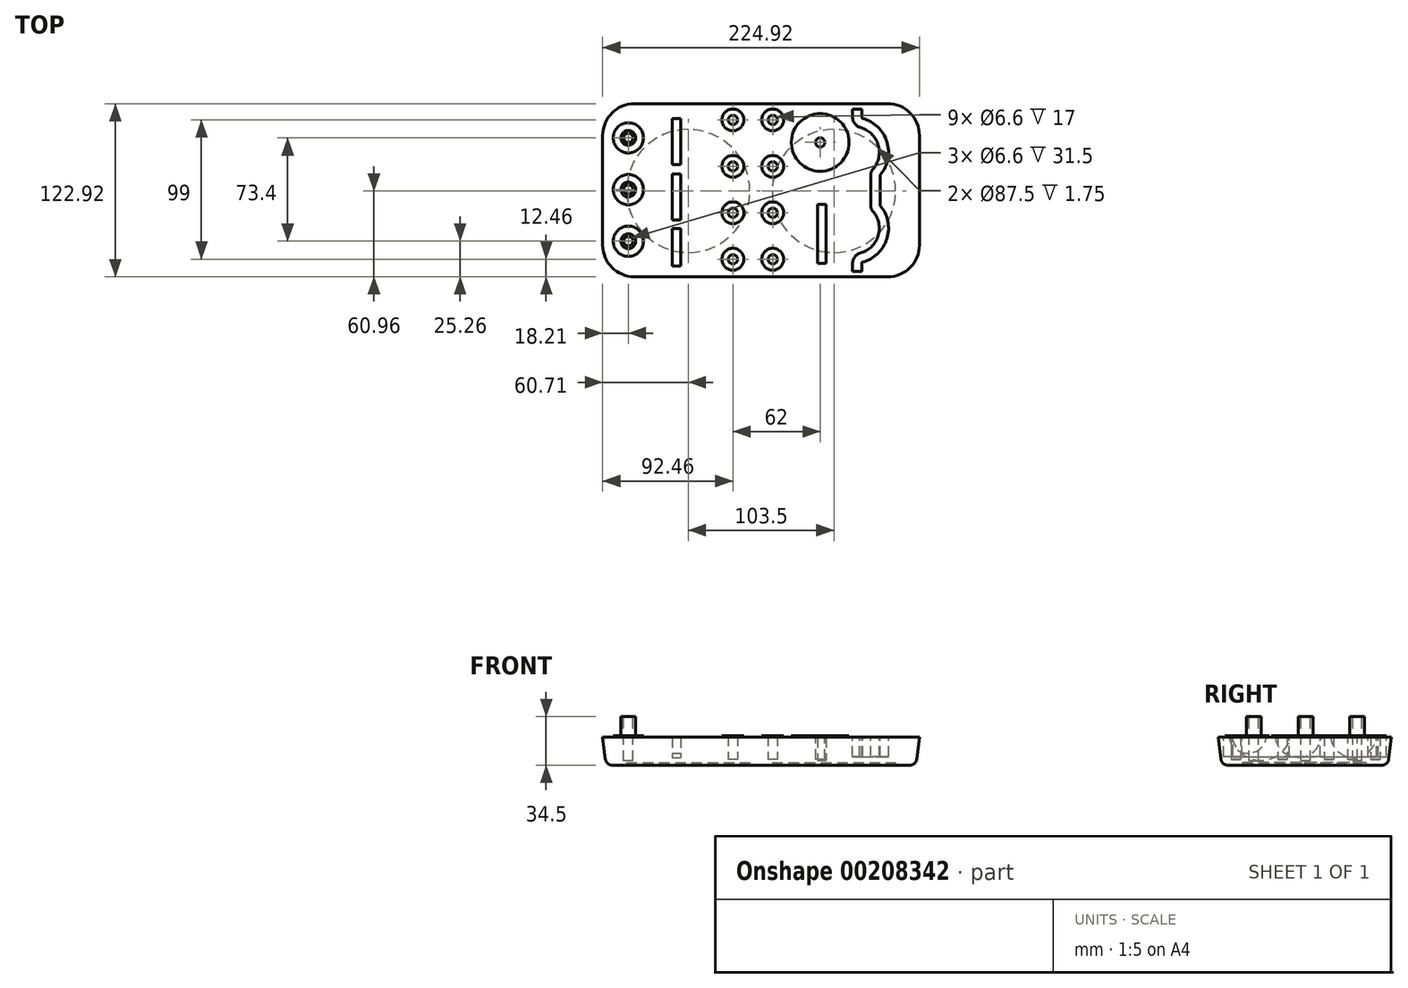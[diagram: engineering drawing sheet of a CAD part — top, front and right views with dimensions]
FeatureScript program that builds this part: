
annotation { "Feature Type Name" : "Feature", "Feature Type Description" : "" }
export const myFeature = defineFeature(function(context is Context, id is Id, definition is map)
    precondition{}
    {
        {
            var Q0;
            Q0=qCreatedBy(makeId("Top.planeOp"),FACE);
            var sketch = newSketch(context, id + "F0", { "sketchPlane" : qUnion([Q0])});
            skLineSegment(sketch, "E0.bottom", {"start": v(20, 0) * mm, "end": v(200, 0) * mm});
            skLineSegment(sketch, "E0.top", {"start": v(20, 118) * mm, "end": v(200, 118) * mm});
            skLineSegment(sketch, "E0.left", {"start": v(0, 20) * mm, "end": v(0, 98) * mm});
            skLineSegment(sketch, "E0.right", {"start": v(220, 20) * mm, "end": v(220, 98) * mm});
            skPoint(sketch, "E1.visualSharp", {"position": v(0, 118) * mm});
            skArc(sketch, "E1.filletArc", {"start": v(20, 118) * mm, "mid": v(5.86, 112.14) * mm, "end": v(0, 98) * mm});
            skPoint(sketch, "E2.visualSharp", {"position": v(220, 118) * mm});
            skArc(sketch, "E2.filletArc", {"start": v(220, 98) * mm, "mid": v(214.14, 112.14) * mm, "end": v(200, 118) * mm});
            skPoint(sketch, "E3.visualSharp", {"position": v(0, 0) * mm});
            skArc(sketch, "E3.filletArc", {"start": v(0, 20) * mm, "mid": v(5.86, 5.86) * mm, "end": v(20, 0) * mm});
            skPoint(sketch, "E4.visualSharp", {"position": v(220, 0) * mm});
            skArc(sketch, "E4.filletArc", {"start": v(200, 0) * mm, "mid": v(214.14, 5.86) * mm, "end": v(220, 20) * mm});
            skSolve(sketch);
        }
        {
            var Q0;
            Q0=makeQuery(id+"F0.imprint","IMPRINT",FACE,{"disambiguationData":[TD([[makeQuery(id+"F0.imprint","IMPRINT",EDGE,{"derivedFrom":sQuery(id+"F0.wireOp",EDGE,"E0.bottom")}),1.0]])]});
            extrude(context, id + "F1", {"entities" : qUnion([Q0]), "depth" : 20 * mm, "hasDraft" : true, "draftAngle" : 7 * degree});
        }
        {
            var Q0;
            Q0=makeQuery(id+"F1.opExtrude","CAP_FACE",FACE,{"disambiguationData":[OSD([sQuery(id+"F0.wireOp",EDGE,"E0.bottom"),sQuery(id+"F0.wireOp",EDGE,"E0.top"),sQuery(id+"F0.wireOp",EDGE,"E0.left"),sQuery(id+"F0.wireOp",EDGE,"E0.right"),sQuery(id+"F0.wireOp",EDGE,"E1.filletArc"),sQuery(id+"F0.wireOp",EDGE,"E2.filletArc"),sQuery(id+"F0.wireOp",EDGE,"E3.filletArc"),sQuery(id+"F0.wireOp",EDGE,"E4.filletArc")])],"isStart":true});
            fillet(context, id + "F2", {"entities" : qUnion([Q0]), "radius" : 5 * mm, "tangentPropagation" : true, "allowEdgeOverflow" : false});
        }
        {
            var Q0;
            Q0=makeQuery(id+"F1.opExtrude","CAP_FACE",FACE,{"disambiguationData":[OSD([sQuery(id+"F0.wireOp",EDGE,"E0.bottom"),sQuery(id+"F0.wireOp",EDGE,"E0.top"),sQuery(id+"F0.wireOp",EDGE,"E0.left"),sQuery(id+"F0.wireOp",EDGE,"E0.right"),sQuery(id+"F0.wireOp",EDGE,"E1.filletArc"),sQuery(id+"F0.wireOp",EDGE,"E2.filletArc"),sQuery(id+"F0.wireOp",EDGE,"E3.filletArc"),sQuery(id+"F0.wireOp",EDGE,"E4.filletArc")])],"isStart":true});
            var sketch = newSketch(context, id + "F3", { "sketchPlane" : qUnion([Q0])});
            skLineSegment(sketch, "E5.bottom", {"start": v(0, 0) * mm, "end": v(58.25, 0) * mm, "construction": true});
            skLineSegment(sketch, "E5.top", {"start": v(0, -58.5) * mm, "end": v(58.25, -58.5) * mm, "construction": true});
            skLineSegment(sketch, "E5.left", {"start": v(0, 0) * mm, "end": v(0, -58.5) * mm, "construction": true});
            skLineSegment(sketch, "E5.right", {"start": v(58.25, 0) * mm, "end": v(58.25, -58.5) * mm, "construction": true});
            skLineSegment(sketch, "E6.bottom", {"start": v(0, 0) * mm, "end": v(161.75, 0) * mm, "construction": true});
            skLineSegment(sketch, "E6.top", {"start": v(0, -58.5) * mm, "end": v(161.75, -58.5) * mm, "construction": true});
            skLineSegment(sketch, "E6.right", {"start": v(161.75, 0) * mm, "end": v(161.75, -58.5) * mm, "construction": true});
            skCircle(sketch, "E7", {"center": v(58.25, -58.5) * mm, "radius": 43.75 * mm});
            skCircle(sketch, "E8", {"center": v(161.75, -58.5) * mm, "radius": 43.75 * mm});
            skSolve(sketch);
        }
        {
            var Q0;
            Q0=qSketchRegion(id+"F3",true);
            extrude(context, id + "F4", {"entities" : qUnion([Q0]), "operationType" : NewBodyOperationType.REMOVE, "oppositeDirection" : true, "depth" : 1.75 * mm});
        }
        {
            var Q0;
            Q0=makeQuery(id+"F1.opExtrude","CAP_FACE",FACE,{"disambiguationData":[OSD([sQuery(id+"F0.wireOp",EDGE,"E0.bottom"),sQuery(id+"F0.wireOp",EDGE,"E0.top"),sQuery(id+"F0.wireOp",EDGE,"E0.left"),sQuery(id+"F0.wireOp",EDGE,"E0.right"),sQuery(id+"F0.wireOp",EDGE,"E1.filletArc"),sQuery(id+"F0.wireOp",EDGE,"E2.filletArc"),sQuery(id+"F0.wireOp",EDGE,"E3.filletArc"),sQuery(id+"F0.wireOp",EDGE,"E4.filletArc")])],"isStart":false});
            var sketch = newSketch(context, id + "F5", { "sketchPlane" : qUnion([Q0])});
            skLineSegment(sketch, "E9.bottom", {"start": v(0, 0) * mm, "end": v(15.75, 0) * mm, "construction": true});
            skLineSegment(sketch, "E9.top", {"start": v(0, 59.5) * mm, "end": v(15.75, 59.5) * mm, "construction": true});
            skLineSegment(sketch, "E9.left", {"start": v(0, 0) * mm, "end": v(0, 59.5) * mm, "construction": true});
            skLineSegment(sketch, "E9.right", {"start": v(15.75, 0) * mm, "end": v(15.75, 59.5) * mm, "construction": true});
            skLineSegment(sketch, "E10", {"start": v(15.75, 59.5) * mm, "end": v(15.75, 22.8) * mm, "construction": true});
            skLineSegment(sketch, "E11", {"start": v(15.75, 59.5) * mm, "end": v(15.75, 96.2) * mm, "construction": true});
            skCircle(sketch, "E12", {"center": v(15.75, 96.2) * mm, "radius": 10.75 * mm});
            skCircle(sketch, "E13", {"center": v(15.75, 59.5) * mm, "radius": 10.75 * mm});
            skCircle(sketch, "E14", {"center": v(15.75, 22.8) * mm, "radius": 10.75 * mm});
            skCircle(sketch, "E15", {"center": v(15.75, 96.2) * mm, "radius": 3.3 * mm});
            skCircle(sketch, "E16", {"center": v(15.75, 96.2) * mm, "radius": 5.25 * mm});
            skCircle(sketch, "E17", {"center": v(15.75, 59.5) * mm, "radius": 5.25 * mm});
            skCircle(sketch, "E18", {"center": v(15.75, 59.5) * mm, "radius": 3.3 * mm});
            skCircle(sketch, "E19", {"center": v(15.75, 22.8) * mm, "radius": 5.25 * mm});
            skCircle(sketch, "E20", {"center": v(15.75, 22.8) * mm, "radius": 3.3 * mm});
            skSolve(sketch);
        }
        {
            var Q0;
            Q0=makeQuery(id+"F5.imprint","IMPRINT",FACE,{"disambiguationData":[TD([[makeQuery(id+"F5.imprint","IMPRINT",EDGE,{"derivedFrom":sQuery(id+"F5.wireOp",EDGE,"E20")}),1.0]])]});
            var Q1;
            Q1=makeQuery(id+"F5.imprint","IMPRINT",FACE,{"disambiguationData":[TD([[makeQuery(id+"F5.imprint","IMPRINT",EDGE,{"derivedFrom":sQuery(id+"F5.wireOp",EDGE,"E18")}),1.0]])]});
            var Q2;
            Q2=makeQuery(id+"F5.imprint","IMPRINT",FACE,{"disambiguationData":[TD([[makeQuery(id+"F5.imprint","IMPRINT",EDGE,{"derivedFrom":sQuery(id+"F5.wireOp",EDGE,"E15")}),1.0]])]});
            extrude(context, id + "F6", {"entities" : qUnion([Q0, Q1, Q2]), "operationType" : NewBodyOperationType.REMOVE, "oppositeDirection" : true, "depth" : 17 * mm});
        }
        {
            var Q0;
            Q0=makeQuery(id+"F5.imprint","IMPRINT",FACE,{"disambiguationData":[TD([[makeQuery(id+"F5.imprint","IMPRINT",EDGE,{"derivedFrom":sQuery(id+"F5.wireOp",EDGE,"E19")}),1.0]])]});
            var Q1;
            Q1=makeQuery(id+"F5.imprint","IMPRINT",FACE,{"disambiguationData":[TD([[makeQuery(id+"F5.imprint","IMPRINT",EDGE,{"derivedFrom":sQuery(id+"F5.wireOp",EDGE,"E17")}),1.0]])]});
            var Q2;
            Q2=makeQuery(id+"F5.imprint","IMPRINT",FACE,{"disambiguationData":[TD([[makeQuery(id+"F5.imprint","IMPRINT",EDGE,{"derivedFrom":sQuery(id+"F5.wireOp",EDGE,"E15")}),-1.0]])]});
            extrude(context, id + "F7", {"entities" : qUnion([Q0, Q1, Q2]), "operationType" : NewBodyOperationType.ADD, "depth" : 14.5 * mm});
        }
        {
            var Q0;
            Q0=makeQuery(id+"F5.imprint","IMPRINT",FACE,{"disambiguationData":[TD([[makeQuery(id+"F5.imprint","IMPRINT",EDGE,{"derivedFrom":sQuery(id+"F5.wireOp",EDGE,"E12")}),1.0]])]});
            var Q1;
            Q1=makeQuery(id+"F5.imprint","IMPRINT",FACE,{"disambiguationData":[TD([[makeQuery(id+"F5.imprint","IMPRINT",EDGE,{"derivedFrom":sQuery(id+"F5.wireOp",EDGE,"E13")}),1.0]])]});
            var Q2;
            Q2=makeQuery(id+"F5.imprint","IMPRINT",FACE,{"disambiguationData":[TD([[makeQuery(id+"F5.imprint","IMPRINT",EDGE,{"derivedFrom":sQuery(id+"F5.wireOp",EDGE,"E14")}),1.0]])]});
            extrude(context, id + "F8", {"entities" : qUnion([Q0, Q1, Q2]), "operationType" : NewBodyOperationType.ADD, "depth" : 1 * mm});
        }
        {
            var Q0;
            Q0=qCreatedBy(makeId("Top.planeOp"),FACE);
            cPlane(context, id + "F9", {"entities" : qUnion([Q0]), "cplaneType" : CPlaneType.OFFSET, "offset" : 22 * mm, "width" : 150 * mm, "height" : 150 * mm});
        }
        {
            var Q0;
            Q0=qCreatedBy(id+"F9.planeOp",FACE);
            var sketch = newSketch(context, id + "F10", { "sketchPlane" : qUnion([Q0])});
            skLineSegment(sketch, "E21.bottom", {"start": v(0, 0) * mm, "end": v(47, 0) * mm, "construction": true});
            skLineSegment(sketch, "E21.top", {"start": v(0, 54.3) * mm, "end": v(47, 54.3) * mm, "construction": true});
            skLineSegment(sketch, "E21.left", {"start": v(0, 0) * mm, "end": v(0, 54.3) * mm, "construction": true});
            skLineSegment(sketch, "E21.right", {"start": v(47, 0) * mm, "end": v(47, 54.3) * mm, "construction": true});
            skLineSegment(sketch, "E22.bottom", {"start": v(47, 54.3) * mm, "end": v(53, 54.3) * mm});
            skLineSegment(sketch, "E22.top", {"start": v(47, 70.8) * mm, "end": v(53, 70.8) * mm});
            skLineSegment(sketch, "E22.left", {"start": v(47, 54.3) * mm, "end": v(47, 70.8) * mm});
            skLineSegment(sketch, "E22.right", {"start": v(53, 54.3) * mm, "end": v(53, 70.8) * mm});
            skSolve(sketch);
        }
        {
            var Q0;
            Q0=makeQuery(id+"F10.imprint","IMPRINT",FACE,{"disambiguationData":[TD([[makeQuery(id+"F10.imprint","IMPRINT",EDGE,{"derivedFrom":sQuery(id+"F10.wireOp",EDGE,"E22.bottom")}),1.0]])]});
            var Q1;
            Q1=sQuery(id+"F10.wireOp",EDGE,"E22.bottom");
            revolve(context, id + "F11", {"operationType" : NewBodyOperationType.REMOVE, "entities" : qUnion([Q0]), "axis" : qUnion([Q1]), "revolveType" : RevolveType.FULL, "oppositeDirection" : true});
        }
        {
            var Q0;
            Q0=qCreatedBy(id+"F9.planeOp",FACE);
            var sketch = newSketch(context, id + "F12", { "sketchPlane" : qUnion([Q0])});
            skLineSegment(sketch, "E23.bottom", {"start": v(0, 0) * mm, "end": v(47, 0) * mm, "construction": true});
            skLineSegment(sketch, "E23.top", {"start": v(0, 18.5) * mm, "end": v(47, 18.5) * mm, "construction": true});
            skLineSegment(sketch, "E23.left", {"start": v(0, 0) * mm, "end": v(0, 18.5) * mm, "construction": true});
            skLineSegment(sketch, "E23.right", {"start": v(47, 0) * mm, "end": v(47, 18.5) * mm, "construction": true});
            skLineSegment(sketch, "E24.bottom", {"start": v(47, 18.5) * mm, "end": v(53, 18.5) * mm});
            skLineSegment(sketch, "E24.top", {"start": v(47, 32) * mm, "end": v(53, 32) * mm});
            skLineSegment(sketch, "E24.left", {"start": v(47, 18.5) * mm, "end": v(47, 32) * mm});
            skLineSegment(sketch, "E24.right", {"start": v(53, 18.5) * mm, "end": v(53, 32) * mm});
            skSolve(sketch);
        }
        {
            var Q0;
            Q0=makeQuery(id+"F12.imprint","IMPRINT",FACE,{"disambiguationData":[TD([[makeQuery(id+"F12.imprint","IMPRINT",EDGE,{"derivedFrom":sQuery(id+"F12.wireOp",EDGE,"E24.bottom")}),1.0]])]});
            var Q1;
            Q1=sQuery(id+"F12.wireOp",EDGE,"E24.bottom");
            revolve(context, id + "F13", {"operationType" : NewBodyOperationType.REMOVE, "entities" : qUnion([Q0]), "axis" : qUnion([Q1]), "revolveType" : RevolveType.FULL, "oppositeDirection" : true});
        }
        {
            var Q0;
            Q0=qCreatedBy(id+"F9.planeOp",FACE);
            var sketch = newSketch(context, id + "F14", { "sketchPlane" : qUnion([Q0])});
            skLineSegment(sketch, "E25.bottom", {"start": v(0, 0) * mm, "end": v(47, 0) * mm, "construction": true});
            skLineSegment(sketch, "E25.top", {"start": v(0, 93.5) * mm, "end": v(47, 93.5) * mm, "construction": true});
            skLineSegment(sketch, "E25.left", {"start": v(0, 0) * mm, "end": v(0, 93.5) * mm, "construction": true});
            skLineSegment(sketch, "E25.right", {"start": v(47, 0) * mm, "end": v(47, 93.5) * mm, "construction": true});
            skLineSegment(sketch, "E26.bottom", {"start": v(47, 93.5) * mm, "end": v(53, 93.5) * mm});
            skLineSegment(sketch, "E26.top", {"start": v(47, 110) * mm, "end": v(53, 110) * mm});
            skLineSegment(sketch, "E26.left", {"start": v(47, 93.5) * mm, "end": v(47, 110) * mm});
            skLineSegment(sketch, "E26.right", {"start": v(53, 93.5) * mm, "end": v(53, 110) * mm});
            skSolve(sketch);
        }
        {
            var Q0;
            Q0=makeQuery(id+"F14.imprint","IMPRINT",FACE,{"disambiguationData":[TD([[makeQuery(id+"F14.imprint","IMPRINT",EDGE,{"derivedFrom":sQuery(id+"F14.wireOp",EDGE,"E26.bottom")}),1.0]])]});
            var Q1;
            Q1=sQuery(id+"F14.wireOp",EDGE,"E26.bottom");
            revolve(context, id + "F15", {"operationType" : NewBodyOperationType.REMOVE, "entities" : qUnion([Q0]), "axis" : qUnion([Q1]), "revolveType" : RevolveType.FULL, "oppositeDirection" : true});
        }
        {
            var Q0;
            Q0=makeQuery(id+"F1.opExtrude","CAP_FACE",FACE,{"disambiguationData":[OSD([sQuery(id+"F0.wireOp",EDGE,"E0.bottom"),sQuery(id+"F0.wireOp",EDGE,"E0.top"),sQuery(id+"F0.wireOp",EDGE,"E0.left"),sQuery(id+"F0.wireOp",EDGE,"E0.right"),sQuery(id+"F0.wireOp",EDGE,"E1.filletArc"),sQuery(id+"F0.wireOp",EDGE,"E2.filletArc"),sQuery(id+"F0.wireOp",EDGE,"E3.filletArc"),sQuery(id+"F0.wireOp",EDGE,"E4.filletArc")])],"isStart":false});
            var sketch = newSketch(context, id + "F16", { "sketchPlane" : qUnion([Q0])});
            skLineSegment(sketch, "E27.bottom", {"start": v(0, 0) * mm, "end": v(90, 0) * mm, "construction": true});
            skLineSegment(sketch, "E27.top", {"start": v(0, 10) * mm, "end": v(90, 10) * mm, "construction": true});
            skLineSegment(sketch, "E27.left", {"start": v(0, 0) * mm, "end": v(0, 10) * mm, "construction": true});
            skLineSegment(sketch, "E27.right", {"start": v(90, 0) * mm, "end": v(90, 10) * mm, "construction": true});
            skLineSegment(sketch, "E28.bottom", {"start": v(90, 10) * mm, "end": v(118.3, 10) * mm, "construction": true});
            skLineSegment(sketch, "E28.top", {"start": v(90, 43) * mm, "end": v(118.3, 43) * mm, "construction": true});
            skLineSegment(sketch, "E28.left", {"start": v(90, 10) * mm, "end": v(90, 43) * mm, "construction": true});
            skLineSegment(sketch, "E28.right", {"start": v(118.3, 10) * mm, "end": v(118.3, 43) * mm, "construction": true});
            skLineSegment(sketch, "E29.top", {"start": v(90, 76) * mm, "end": v(118.3, 76) * mm, "construction": true});
            skLineSegment(sketch, "E29.left", {"start": v(90, 43) * mm, "end": v(90, 76) * mm, "construction": true});
            skLineSegment(sketch, "E29.right", {"start": v(118.3, 43) * mm, "end": v(118.3, 76) * mm, "construction": true});
            skLineSegment(sketch, "E30.top", {"start": v(90, 109) * mm, "end": v(118.3, 109) * mm, "construction": true});
            skLineSegment(sketch, "E30.left", {"start": v(90, 76) * mm, "end": v(90, 109) * mm, "construction": true});
            skLineSegment(sketch, "E30.right", {"start": v(118.3, 76) * mm, "end": v(118.3, 109) * mm, "construction": true});
            skCircle(sketch, "E31", {"center": v(90, 109) * mm, "radius": 3.3 * mm});
            skCircle(sketch, "E32", {"center": v(118.3, 109) * mm, "radius": 3.3 * mm});
            skCircle(sketch, "E33", {"center": v(118.3, 76) * mm, "radius": 3.3 * mm});
            skCircle(sketch, "E34", {"center": v(90, 76) * mm, "radius": 3.3 * mm});
            skCircle(sketch, "E35", {"center": v(90, 43) * mm, "radius": 3.3 * mm});
            skCircle(sketch, "E36", {"center": v(118.3, 43) * mm, "radius": 3.3 * mm});
            skCircle(sketch, "E37", {"center": v(118.3, 10) * mm, "radius": 3.3 * mm});
            skCircle(sketch, "E38", {"center": v(90, 10) * mm, "radius": 3.3 * mm});
            skCircle(sketch, "E39", {"center": v(90, 109) * mm, "radius": 7.75 * mm});
            skCircle(sketch, "E40", {"center": v(118.3, 109) * mm, "radius": 7.75 * mm});
            skCircle(sketch, "E41", {"center": v(118.3, 76) * mm, "radius": 7.75 * mm});
            skCircle(sketch, "E42", {"center": v(90, 76) * mm, "radius": 7.75 * mm});
            skCircle(sketch, "E43", {"center": v(90, 43) * mm, "radius": 7.75 * mm});
            skCircle(sketch, "E44", {"center": v(118.3, 43) * mm, "radius": 7.75 * mm});
            skCircle(sketch, "E45", {"center": v(118.3, 10) * mm, "radius": 7.75 * mm});
            skCircle(sketch, "E46", {"center": v(90, 10) * mm, "radius": 7.75 * mm});
            skSolve(sketch);
        }
        {
            var Q0;
            Q0=makeQuery(id+"F16.imprint","IMPRINT",FACE,{"disambiguationData":[TD([[makeQuery(id+"F16.imprint","IMPRINT",EDGE,{"derivedFrom":sQuery(id+"F16.wireOp",EDGE,"E31")}),-1.0]])]});
            var Q1;
            Q1=makeQuery(id+"F16.imprint","IMPRINT",FACE,{"disambiguationData":[TD([[makeQuery(id+"F16.imprint","IMPRINT",EDGE,{"derivedFrom":sQuery(id+"F16.wireOp",EDGE,"E32")}),-1.0]])]});
            var Q2;
            Q2=makeQuery(id+"F16.imprint","IMPRINT",FACE,{"disambiguationData":[TD([[makeQuery(id+"F16.imprint","IMPRINT",EDGE,{"derivedFrom":sQuery(id+"F16.wireOp",EDGE,"E33")}),-1.0]])]});
            var Q3;
            Q3=makeQuery(id+"F16.imprint","IMPRINT",FACE,{"disambiguationData":[TD([[makeQuery(id+"F16.imprint","IMPRINT",EDGE,{"derivedFrom":sQuery(id+"F16.wireOp",EDGE,"E34")}),-1.0]])]});
            var Q4;
            Q4=makeQuery(id+"F16.imprint","IMPRINT",FACE,{"disambiguationData":[TD([[makeQuery(id+"F16.imprint","IMPRINT",EDGE,{"derivedFrom":sQuery(id+"F16.wireOp",EDGE,"E35")}),-1.0]])]});
            var Q5;
            Q5=makeQuery(id+"F16.imprint","IMPRINT",FACE,{"disambiguationData":[TD([[makeQuery(id+"F16.imprint","IMPRINT",EDGE,{"derivedFrom":sQuery(id+"F16.wireOp",EDGE,"E36")}),-1.0]])]});
            var Q6;
            Q6=makeQuery(id+"F16.imprint","IMPRINT",FACE,{"disambiguationData":[TD([[makeQuery(id+"F16.imprint","IMPRINT",EDGE,{"derivedFrom":sQuery(id+"F16.wireOp",EDGE,"E37")}),-1.0]])]});
            var Q7;
            Q7=makeQuery(id+"F16.imprint","IMPRINT",FACE,{"disambiguationData":[TD([[makeQuery(id+"F16.imprint","IMPRINT",EDGE,{"derivedFrom":sQuery(id+"F16.wireOp",EDGE,"E38")}),-1.0]])]});
            extrude(context, id + "F17", {"entities" : qUnion([Q0, Q1, Q2, Q3, Q4, Q5, Q6, Q7]), "operationType" : NewBodyOperationType.ADD, "depth" : 1 * mm});
        }
        {
            var Q0;
            Q0=makeQuery(id+"F16.imprint","IMPRINT",FACE,{"disambiguationData":[TD([[makeQuery(id+"F16.imprint","IMPRINT",EDGE,{"derivedFrom":sQuery(id+"F16.wireOp",EDGE,"E31")}),1.0]])]});
            var Q1;
            Q1=makeQuery(id+"F16.imprint","IMPRINT",FACE,{"disambiguationData":[TD([[makeQuery(id+"F16.imprint","IMPRINT",EDGE,{"derivedFrom":sQuery(id+"F16.wireOp",EDGE,"E32")}),1.0]])]});
            var Q2;
            Q2=makeQuery(id+"F16.imprint","IMPRINT",FACE,{"disambiguationData":[TD([[makeQuery(id+"F16.imprint","IMPRINT",EDGE,{"derivedFrom":sQuery(id+"F16.wireOp",EDGE,"E34")}),1.0]])]});
            var Q3;
            Q3=makeQuery(id+"F16.imprint","IMPRINT",FACE,{"disambiguationData":[TD([[makeQuery(id+"F16.imprint","IMPRINT",EDGE,{"derivedFrom":sQuery(id+"F16.wireOp",EDGE,"E33")}),1.0]])]});
            var Q4;
            Q4=makeQuery(id+"F16.imprint","IMPRINT",FACE,{"disambiguationData":[TD([[makeQuery(id+"F16.imprint","IMPRINT",EDGE,{"derivedFrom":sQuery(id+"F16.wireOp",EDGE,"E36")}),1.0]])]});
            var Q5;
            Q5=makeQuery(id+"F16.imprint","IMPRINT",FACE,{"disambiguationData":[TD([[makeQuery(id+"F16.imprint","IMPRINT",EDGE,{"derivedFrom":sQuery(id+"F16.wireOp",EDGE,"E35")}),1.0]])]});
            var Q6;
            Q6=makeQuery(id+"F16.imprint","IMPRINT",FACE,{"disambiguationData":[TD([[makeQuery(id+"F16.imprint","IMPRINT",EDGE,{"derivedFrom":sQuery(id+"F16.wireOp",EDGE,"E38")}),1.0]])]});
            var Q7;
            Q7=makeQuery(id+"F16.imprint","IMPRINT",FACE,{"disambiguationData":[TD([[makeQuery(id+"F16.imprint","IMPRINT",EDGE,{"derivedFrom":sQuery(id+"F16.wireOp",EDGE,"E37")}),1.0]])]});
            extrude(context, id + "F18", {"entities" : qUnion([Q0, Q1, Q2, Q3, Q4, Q5, Q6, Q7]), "operationType" : NewBodyOperationType.REMOVE, "oppositeDirection" : true, "depth" : 16 * mm});
        }
        {
            var Q0;
            Q0=qCreatedBy(makeId("Top.planeOp"),FACE);
            cPlane(context, id + "F19", {"entities" : qUnion([Q0]), "cplaneType" : CPlaneType.OFFSET, "offset" : 25 * mm, "width" : 150 * mm, "height" : 150 * mm});
        }
        {
            var Q0;
            Q0=qCreatedBy(id+"F19.planeOp",FACE);
            var sketch = newSketch(context, id + "F20", { "sketchPlane" : qUnion([Q0])});
            skLineSegment(sketch, "E47.bottom", {"start": v(0, 0) * mm, "end": v(150, 0) * mm, "construction": true});
            skLineSegment(sketch, "E47.top", {"start": v(0, 28) * mm, "end": v(150, 28) * mm, "construction": true});
            skLineSegment(sketch, "E47.left", {"start": v(0, 0) * mm, "end": v(0, 28) * mm, "construction": true});
            skLineSegment(sketch, "E47.right", {"start": v(150, 0) * mm, "end": v(150, 28) * mm, "construction": true});
            skLineSegment(sketch, "E48.bottom", {"start": v(150, 28) * mm, "end": v(156, 28) * mm});
            skLineSegment(sketch, "E48.top", {"start": v(150, 49.5) * mm, "end": v(156, 49.5) * mm});
            skLineSegment(sketch, "E48.left", {"start": v(150, 28) * mm, "end": v(150, 49.5) * mm});
            skLineSegment(sketch, "E48.right", {"start": v(156, 28) * mm, "end": v(156, 49.5) * mm});
            skSolve(sketch);
        }
        {
            var Q0;
            Q0=makeQuery(id+"F20.imprint","IMPRINT",FACE,{"disambiguationData":[TD([[makeQuery(id+"F20.imprint","IMPRINT",EDGE,{"derivedFrom":sQuery(id+"F20.wireOp",EDGE,"E48.bottom")}),1.0]])]});
            var Q1;
            Q1=sQuery(id+"F20.wireOp",EDGE,"E48.bottom");
            revolve(context, id + "F21", {"operationType" : NewBodyOperationType.REMOVE, "entities" : qUnion([Q0]), "axis" : qUnion([Q1]), "revolveType" : RevolveType.FULL, "oppositeDirection" : true});
        }
        {
            var Q0;
            {var subQ0=sQuery(id+"F0.wireOp",EDGE,"E0.left");var subQ1=sQuery(id+"F0.wireOp",EDGE,"E0.right");var subQ2=sQuery(id+"F0.wireOp",EDGE,"E0.top");var subQ3=sQuery(id+"F0.wireOp",EDGE,"E0.bottom");var subQ4=sQuery(id+"F0.wireOp",EDGE,"E1.filletArc");var subQ5=sQuery(id+"F0.wireOp",EDGE,"E2.filletArc");var subQ6=sQuery(id+"F0.wireOp",EDGE,"E3.filletArc");var subQ7=sQuery(id+"F0.wireOp",EDGE,"E4.filletArc");Q0=makeQuery(id+"F17.boolean.opBoolean","SPLIT",FACE,{"disambiguationData":[TD([makeQuery(id+"F1.opExtrude","SWEPT_FACE",FACE,{"disambiguationData":[OSD([subQ3])]})])],"derivedFrom":makeQuery(id+"F1.opExtrude","CAP_FACE",FACE,{"disambiguationData":[OSD([subQ3,subQ2,subQ0,subQ1,subQ4,subQ5,subQ6,subQ7])],"isStart":false})});}
            var sketch = newSketch(context, id + "F22", { "sketchPlane" : qUnion([Q0])});
            skLineSegment(sketch, "E49.bottom", {"start": v(0, 0) * mm, "end": v(152, 0) * mm, "construction": true});
            skLineSegment(sketch, "E49.top", {"start": v(0, 93) * mm, "end": v(152, 93) * mm, "construction": true});
            skLineSegment(sketch, "E49.left", {"start": v(0, 0) * mm, "end": v(0, 93) * mm, "construction": true});
            skLineSegment(sketch, "E49.right", {"start": v(152, 0) * mm, "end": v(152, 93) * mm, "construction": true});
            skCircle(sketch, "E50", {"center": v(152, 93) * mm, "radius": 3.3 * mm});
            skCircle(sketch, "E51", {"center": v(152, 93) * mm, "radius": 20.5 * mm});
            skSolve(sketch);
        }
        {
            var Q0;
            Q0=makeQuery(id+"F22.imprint","IMPRINT",FACE,{"disambiguationData":[TD([[makeQuery(id+"F22.imprint","IMPRINT",EDGE,{"derivedFrom":sQuery(id+"F22.wireOp",EDGE,"E50")}),1.0]])]});
            extrude(context, id + "F23", {"entities" : qUnion([Q0]), "operationType" : NewBodyOperationType.REMOVE, "oppositeDirection" : true, "depth" : 16 * mm});
        }
        {
            var Q0;
            Q0=makeQuery(id+"F22.imprint","IMPRINT",FACE,{"disambiguationData":[TD([[makeQuery(id+"F22.imprint","IMPRINT",EDGE,{"derivedFrom":sQuery(id+"F22.wireOp",EDGE,"E50")}),-1.0]])]});
            extrude(context, id + "F24", {"entities" : qUnion([Q0]), "operationType" : NewBodyOperationType.ADD, "depth" : 1 * mm});
        }
        {
            var Q0;
            {var subQ0=sQuery(id+"F0.wireOp",EDGE,"E0.left");var subQ1=sQuery(id+"F0.wireOp",EDGE,"E0.right");var subQ2=sQuery(id+"F0.wireOp",EDGE,"E0.top");var subQ3=sQuery(id+"F0.wireOp",EDGE,"E0.bottom");var subQ4=sQuery(id+"F0.wireOp",EDGE,"E1.filletArc");var subQ5=sQuery(id+"F0.wireOp",EDGE,"E2.filletArc");var subQ6=sQuery(id+"F0.wireOp",EDGE,"E3.filletArc");var subQ7=sQuery(id+"F0.wireOp",EDGE,"E4.filletArc");Q0=makeQuery(id+"F17.boolean.opBoolean","SPLIT",FACE,{"disambiguationData":[TD([makeQuery(id+"F1.opExtrude","SWEPT_FACE",FACE,{"disambiguationData":[OSD([subQ3])]})])],"derivedFrom":makeQuery(id+"F1.opExtrude","CAP_FACE",FACE,{"disambiguationData":[OSD([subQ3,subQ2,subQ0,subQ1,subQ4,subQ5,subQ6,subQ7])],"isStart":false})});}
            var sketch = newSketch(context, id + "F25", { "sketchPlane" : qUnion([Q0])});
            skLineSegment(sketch, "E52.bottom", {"start": v(0, 0) * mm, "end": v(188, 0) * mm, "construction": true});
            skLineSegment(sketch, "E52.top", {"start": v(0, 59) * mm, "end": v(188, 59) * mm, "construction": true});
            skLineSegment(sketch, "E52.left", {"start": v(0, 0) * mm, "end": v(0, 59) * mm, "construction": true});
            skLineSegment(sketch, "E53.bottom", {"start": v(188, 59) * mm, "end": v(175.6, 59) * mm, "construction": true});
            skLineSegment(sketch, "E53.top", {"start": v(188, 32) * mm, "end": v(175.6, 32) * mm, "construction": true});
            skLineSegment(sketch, "E53.right", {"start": v(175.6, 59) * mm, "end": v(175.6, 32) * mm, "construction": true});
            skArc(sketch, "E54", {"start": v(179.88, 14.2) * mm, "mid": v(193.06, 26.53) * mm, "end": v(189.27, 44.17) * mm});
            skLineSegment(sketch, "E55.bottom", {"start": v(188, 59) * mm, "end": v(184.5, 59) * mm, "construction": true});
            skLineSegment(sketch, "E55.top", {"start": v(188, 6.8) * mm, "end": v(184.5, 6.8) * mm, "construction": true});
            skLineSegment(sketch, "E55.right", {"start": v(184.5, 59) * mm, "end": v(184.5, 6.8) * mm, "construction": true});
            skLineSegment(sketch, "E56.bottom", {"start": v(188, 59) * mm, "end": v(174.65, 59) * mm, "construction": true});
            skLineSegment(sketch, "E56.top", {"start": v(188, 7.25) * mm, "end": v(174.65, 7.25) * mm, "construction": true});
            skLineSegment(sketch, "E56.right", {"start": v(174.65, 59) * mm, "end": v(174.65, 7.25) * mm, "construction": true});
            skLineSegment(sketch, "E57", {"start": v(174.91, 7.25) * mm, "end": v(174.91, 5.25) * mm});
            skArc(sketch, "E58.trimOffspring", {"start": v(179.88, 14.2) * mm, "mid": v(176.39, 11.45) * mm, "end": v(174.91, 7.25) * mm});
            skArc(sketch, "E59.trimOffspring", {"start": v(175.6, 50.3) * mm, "mid": v(175.12, 50.3) * mm, "end": v(174.65, 50.28) * mm});
            skLineSegment(sketch, "E60", {"start": v(188, 59) * mm, "end": v(188, 52.4) * mm});
            skLineSegment(sketch, "E61", {"start": v(188, 52.4) * mm, "end": v(188, 47.5) * mm});
            skArc(sketch, "E62.filletArc", {"start": v(188, 47.5) * mm, "mid": v(188.33, 45.72) * mm, "end": v(189.27, 44.17) * mm});
            skLineSegment(sketch, "E63.0", {"start": v(181.51, 6.99) * mm, "end": v(181.51, 5.25) * mm});
            skLineSegment(sketch, "E63.1", {"start": v(194.6, 59) * mm, "end": v(194.6, 52.4) * mm});
            skLineSegment(sketch, "E63.2", {"start": v(194.6, 52.4) * mm, "end": v(194.6, 48.1) * mm});
            skArc(sketch, "E63.3", {"start": v(182.14, 7.97) * mm, "mid": v(199.38, 24.61) * mm, "end": v(194.6, 48.1) * mm});
            skArc(sketch, "E63.4", {"start": v(182.14, 7.97) * mm, "mid": v(181.72, 7.55) * mm, "end": v(181.51, 6.99) * mm});
            skLineSegment(sketch, "E64.MirrorCS", {"start": v(188, 59) * mm, "end": v(188, 65.6) * mm});
            skLineSegment(sketch, "E65.MirrorCS", {"start": v(188, 65.6) * mm, "end": v(188, 70.5) * mm});
            skArc(sketch, "E66.MirrorCS", {"start": v(188, 70.5) * mm, "mid": v(188.33, 72.28) * mm, "end": v(189.27, 73.83) * mm});
            skArc(sketch, "E67.MirrorCS", {"start": v(179.88, 103.8) * mm, "mid": v(193.06, 91.47) * mm, "end": v(189.27, 73.83) * mm});
            skArc(sketch, "E68.MirrorCS", {"start": v(179.88, 103.8) * mm, "mid": v(176.39, 106.55) * mm, "end": v(174.91, 110.75) * mm});
            skLineSegment(sketch, "E69.MirrorCS", {"start": v(174.91, 110.75) * mm, "end": v(174.91, 112.75) * mm});
            skLineSegment(sketch, "E70.MirrorCS", {"start": v(181.51, 111.01) * mm, "end": v(181.51, 112.75) * mm});
            skArc(sketch, "E71.MirrorCS", {"start": v(182.14, 110.03) * mm, "mid": v(181.72, 110.45) * mm, "end": v(181.51, 111.01) * mm});
            skArc(sketch, "E72.MirrorCS", {"start": v(182.14, 110.03) * mm, "mid": v(199.38, 93.39) * mm, "end": v(194.6, 69.9) * mm});
            skLineSegment(sketch, "E73.MirrorCS", {"start": v(194.6, 65.6) * mm, "end": v(194.6, 69.9) * mm});
            skLineSegment(sketch, "E74.MirrorCS", {"start": v(194.6, 59) * mm, "end": v(194.6, 65.6) * mm});
            skLineSegment(sketch, "E75.top", {"start": v(174.91, 116.75) * mm, "end": v(181.51, 116.75) * mm});
            skLineSegment(sketch, "E75.left", {"start": v(174.91, 112.75) * mm, "end": v(174.91, 116.75) * mm});
            skLineSegment(sketch, "E75.right", {"start": v(181.51, 112.75) * mm, "end": v(181.51, 116.75) * mm});
            skLineSegment(sketch, "E76.top", {"start": v(174.91, 1.25) * mm, "end": v(181.51, 1.25) * mm});
            skLineSegment(sketch, "E76.left", {"start": v(174.91, 5.25) * mm, "end": v(174.91, 1.25) * mm});
            skLineSegment(sketch, "E76.right", {"start": v(181.51, 5.25) * mm, "end": v(181.51, 1.25) * mm});
            skSolve(sketch);
        }
        {
            var Q0;
            Q0=makeQuery(id+"F25.imprint","IMPRINT",FACE,{"disambiguationData":[TD([[makeQuery(id+"F25.imprint","IMPRINT",EDGE,{"derivedFrom":sQuery(id+"F25.wireOp",EDGE,"E54")}),-1.0]])]});
            extrude(context, id + "F26", {"entities" : qUnion([Q0]), "operationType" : NewBodyOperationType.REMOVE, "oppositeDirection" : true, "depth" : 14 * mm});
        }
    });
